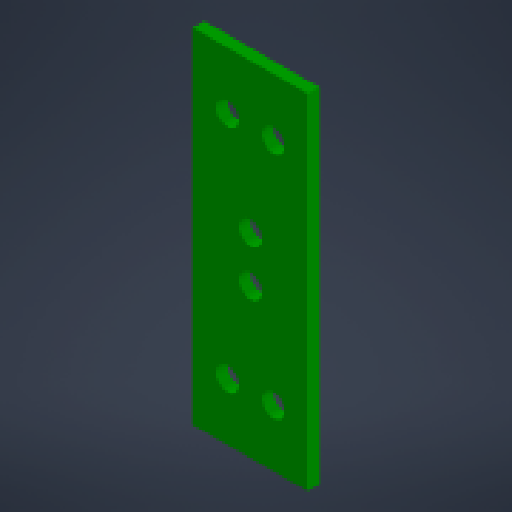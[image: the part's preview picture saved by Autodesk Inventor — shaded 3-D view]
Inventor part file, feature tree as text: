
AUTODESK INVENTOR PART (.ipt)
format: ipt  version: 2024 (Build 280153000, 153)  size: 147,968 bytes
history: native  units: mm
features: other x6, reference x6, extrude x2, sketch x2
ambient origin geometry x8: Origin, YZ Plane, XZ Plane, XY Plane, X Axis, Y Axis, Z Axis, Center Point
bodies: Body1 (feature_tree)
feature tree (16):
  other  "Твердое тело1"
  extrude  "Выдавливание1"  Depth=60.0mm
  extrude  "Выдавливание2"  Depth=20.0mm
  sketch  "Эскиз2"
  sketch  "Эскиз3"
  reference  "Ссылка1"
  reference  "Ссылка2"
  reference  "Ссылка3"
  reference  "Ссылка4"
  reference  "Ссылка5"
  reference  "Ссылка6"
  parser-record x1  (decoder bookkeeping rows leaked as tree rows — omitted from the tree; the rows remain in map.json)
  other  "base_assembly.iam"
  other  "side_section:1"
  other  "main axis:1"
  other  "side_section:2"
note: 1 file-system path scrubbed to <path> (originals preserved in map.json)
